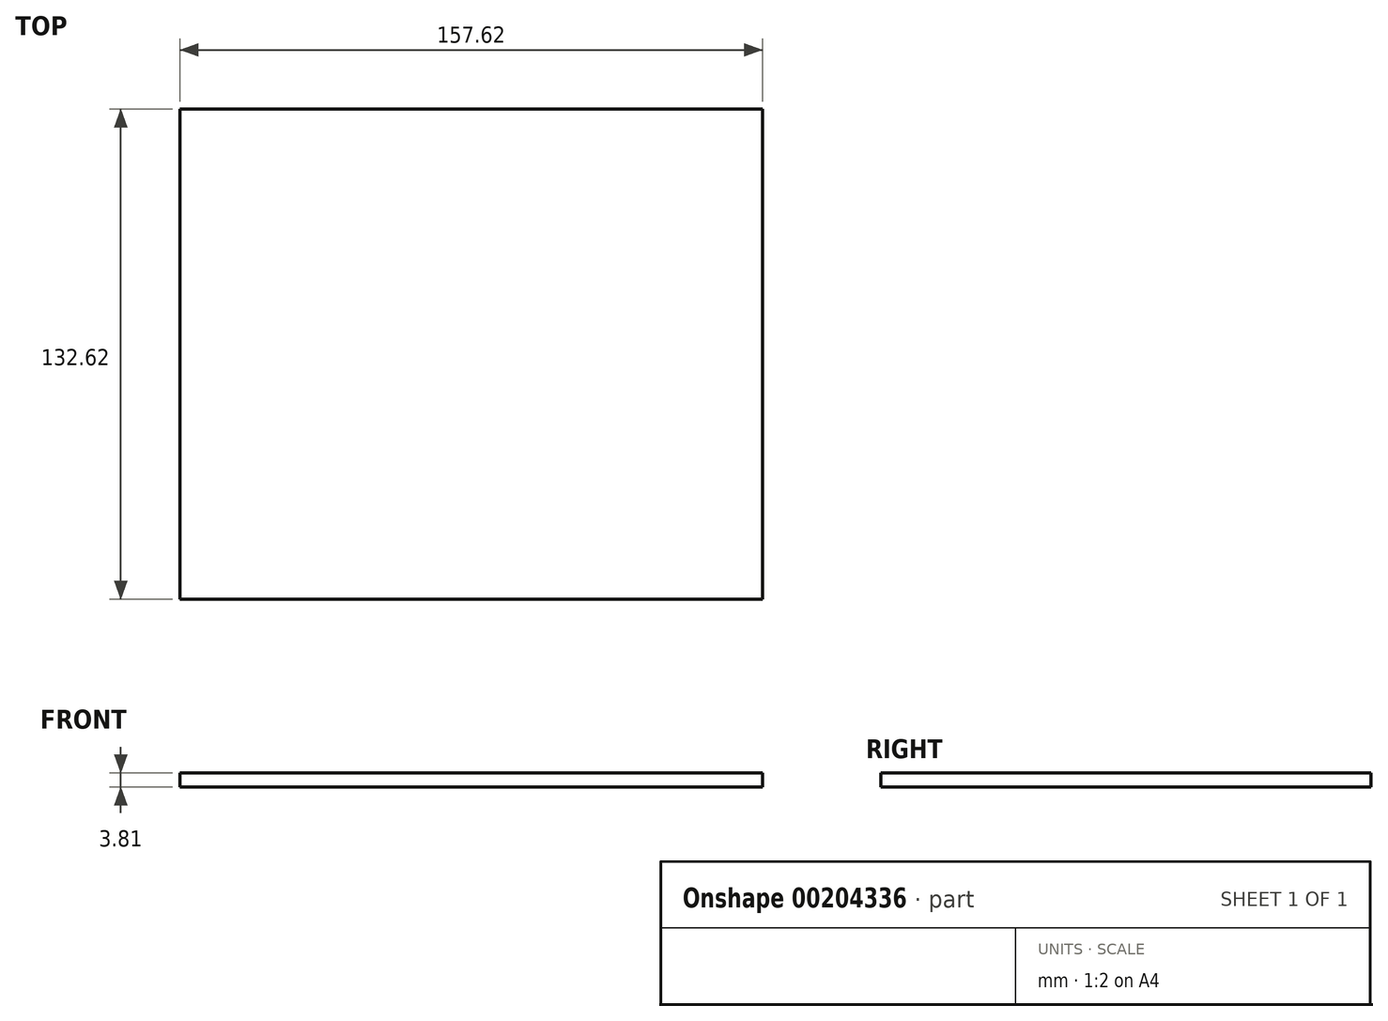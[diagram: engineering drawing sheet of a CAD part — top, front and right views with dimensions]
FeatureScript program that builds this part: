
annotation { "Feature Type Name" : "Feature", "Feature Type Description" : "" }
export const myFeature = defineFeature(function(context is Context, id is Id, definition is map)
    precondition{}
    {
        {
            var Q0;
            Q0=qCreatedBy(makeId("Top.planeOp"),FACE);
            var sketch = newSketch(context, id + "F0", { "sketchPlane" : qUnion([Q0])});
            skLineSegment(sketch, "E0.bottom", {"start": v(78.8, 66.3) * mm, "end": v(-78.8, 66.3) * mm});
            skLineSegment(sketch, "E0.top", {"start": v(78.8, -66.3) * mm, "end": v(-78.8, -66.3) * mm});
            skLineSegment(sketch, "E0.left", {"start": v(78.8, 66.31) * mm, "end": v(78.8, -66.3) * mm});
            skLineSegment(sketch, "E0.right", {"start": v(-78.8, 66.31) * mm, "end": v(-78.8, -66.3) * mm});
            skPoint(sketch, "E0.middle", {"position": v(0, 0) * mm});
            skSolve(sketch);
        }
        {
            var Q0;
            Q0 = qSketchRegion(id + "F0", true);
            extrude(context, id + "F1", {"entities" : qUnion([Q0]), "depth" : 3.8 * mm});
        }
    });
